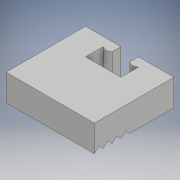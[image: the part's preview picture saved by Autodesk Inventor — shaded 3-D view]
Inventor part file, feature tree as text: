
AUTODESK INVENTOR PART (.ipt)
format: ipt  version: 2017 (Build 210142000, 142)  size: 142,336 bytes
history: native  units: mm
features: extrude x4, sketch x3
ambient origin geometry x8: Origin, YZ Plane, XZ Plane, XY Plane, X Axis, Y Axis, Z Axis, Center Point
bodies: Solid1 (feature_tree)
feature tree (7):
  extrude  "Extrusion1"  Depth=9.0mm
  extrude  "Extrusion10"  Depth=3.0mm
  extrude  "Extrusion13"  Depth=2.0mm
  extrude  "Extrusion14"  Depth=4.0mm
  sketch  "Sketch1"  dims[d0=10.0mm d1=9.0mm]
  sketch  "Sketch12"  dims[d2=3.0mm d3=0.0mm d23=0.5mm]
  sketch  "Sketch16"  dims[d24=6.0mm d47=2.0mm d48=4.0mm d49=2.0mm d50=2.0mm d51=10.0mm d52=0.0mm d66=10.0mm d67=0.0mm d68=5.0mm d69=0.75mm d70=0.75mm d71=10.0mm d72=0.0mm]
